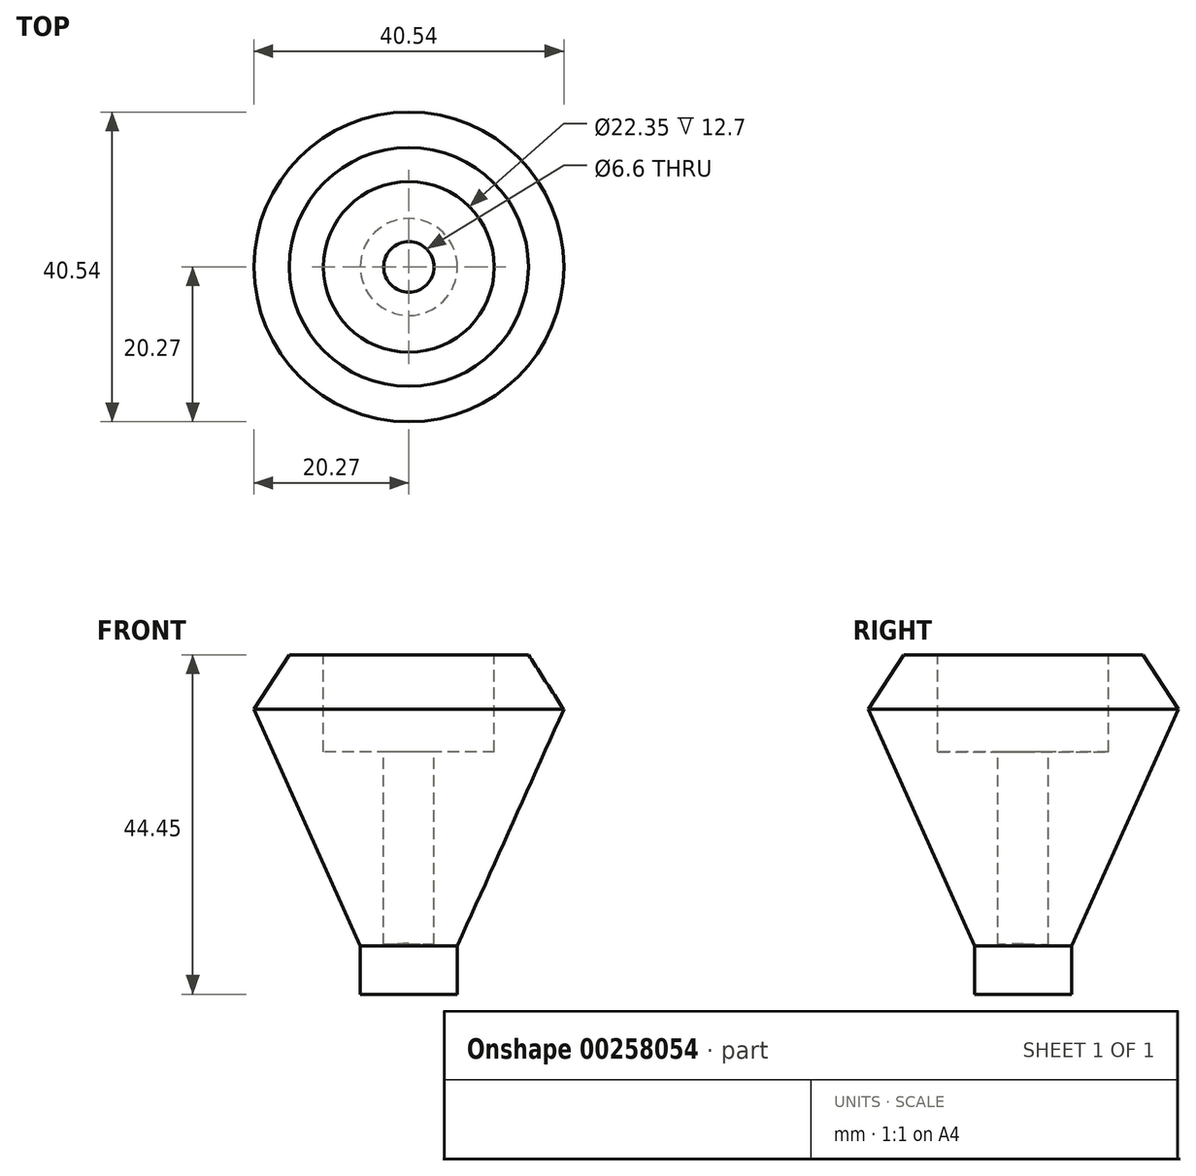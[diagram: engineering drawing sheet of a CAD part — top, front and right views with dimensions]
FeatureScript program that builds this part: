
annotation { "Feature Type Name" : "Feature", "Feature Type Description" : "" }
export const myFeature = defineFeature(function(context is Context, id is Id, definition is map)
    precondition{}
    {
        {
            var Q0;
            Q0=qCreatedBy(makeId("Right.planeOp"),FACE);
            var sketch = newSketch(context, id + "F0", { "sketchPlane" : qUnion([Q0])});
            skLineSegment(sketch, "E0", {"start": v(3.3, 21.19) * mm, "end": v(3.3, -23.26) * mm});
            skLineSegment(sketch, "E1", {"start": v(3.3, -23.26) * mm, "end": v(6.35, -23.26) * mm});
            skLineSegment(sketch, "E2", {"start": v(3.3, 21.19) * mm, "end": v(23.5, 21.19) * mm});
            skLineSegment(sketch, "E3", {"start": v(23.5, 21.19) * mm, "end": v(6.35, -16.91) * mm});
            skLineSegment(sketch, "E4", {"start": v(6.35, -16.91) * mm, "end": v(6.35, -23.26) * mm});
            skLineSegment(sketch, "E5", {"start": v(0, 58.06) * mm, "end": v(0, -48.62) * mm, "construction": true});
            skLineSegment(sketch, "E6", {"start": v(3.3, -23.26) * mm, "end": v(0, -23.26) * mm});
            skLineSegment(sketch, "E7", {"start": v(0, -23.26) * mm, "end": v(0, -16.61) * mm});
            skLineSegment(sketch, "E8", {"start": v(0, -16.61) * mm, "end": v(6.35, -16.91) * mm});
            skSolve(sketch);
        }
        {
            var Q0;
            {var subQ0=sQuery(id+"F0.wireOp",EDGE,"E2");Q0=makeQuery(id+"F0.imprint","IMPRINT",FACE,{"disambiguationData":[TD([[makeQuery(id+"F0.imprint","IMPRINT",EDGE,{"derivedFrom":subQ0}),-1.0]])]});}
            var Q1;
            {var subQ0=sQuery(id+"F0.wireOp",EDGE,"E1");Q1=makeQuery(id+"F0.imprint","IMPRINT",FACE,{"disambiguationData":[TD([[makeQuery(id+"F0.imprint","IMPRINT",EDGE,{"derivedFrom":subQ0}),1.0]])]});}
            var Q2;
            {var subQ0=sQuery(id+"F0.wireOp",EDGE,"E6");Q2=makeQuery(id+"F0.imprint","IMPRINT",FACE,{"disambiguationData":[TD([[makeQuery(id+"F0.imprint","IMPRINT",EDGE,{"derivedFrom":subQ0}),-1.0]])]});}
            var Q3;
            Q3=sQuery(id+"F0.wireOp",EDGE,"E5");
            revolve(context, id + "F1", {"entities" : qUnion([Q0, Q1, Q2]), "axis" : qUnion([Q3]), "revolveType" : RevolveType.FULL});
        }
        {
            var Q0;
            Q0=makeQuery(id+"F1.opRevolve","SWEPT_FACE",FACE,{"disambiguationData":[OSD([sQuery(id+"F0.wireOp",EDGE,"E2")])]});
            var sketch = newSketch(context, id + "F2", { "sketchPlane" : qUnion([Q0])});
            skCircle(sketch, "E9", {"center": v(0, 0) * mm, "radius": 11.18 * mm});
            skSolve(sketch);
        }
        {
            var Q0;
            Q0=makeQuery(id+"F2.imprint","IMPRINT",FACE,{"disambiguationData":[TD([[makeQuery(id+"F2.imprint","IMPRINT",EDGE,{"derivedFrom":sQuery(id+"F2.wireOp",EDGE,"E9")}),1.0]])]});
            extrude(context, id + "F3", {"entities" : qUnion([Q0]), "operationType" : NewBodyOperationType.REMOVE, "oppositeDirection" : true, "depth" : 12.7 * mm});
        }
        {
            var Q0;
            Q0=makeQuery(id+"F1.opRevolve","SWEPT_EDGE",EDGE,{"disambiguationData":[OSD([sQuery(id+"F0.wireOp",EDGE,"E2"),sQuery(id+"F0.wireOp",EDGE,"E3")])]});
            chamfer(context, id + "F4", {"entities" : qUnion([Q0]), "width" : 5.08 * mm, "tangentPropagation" : true});
        }
    });
